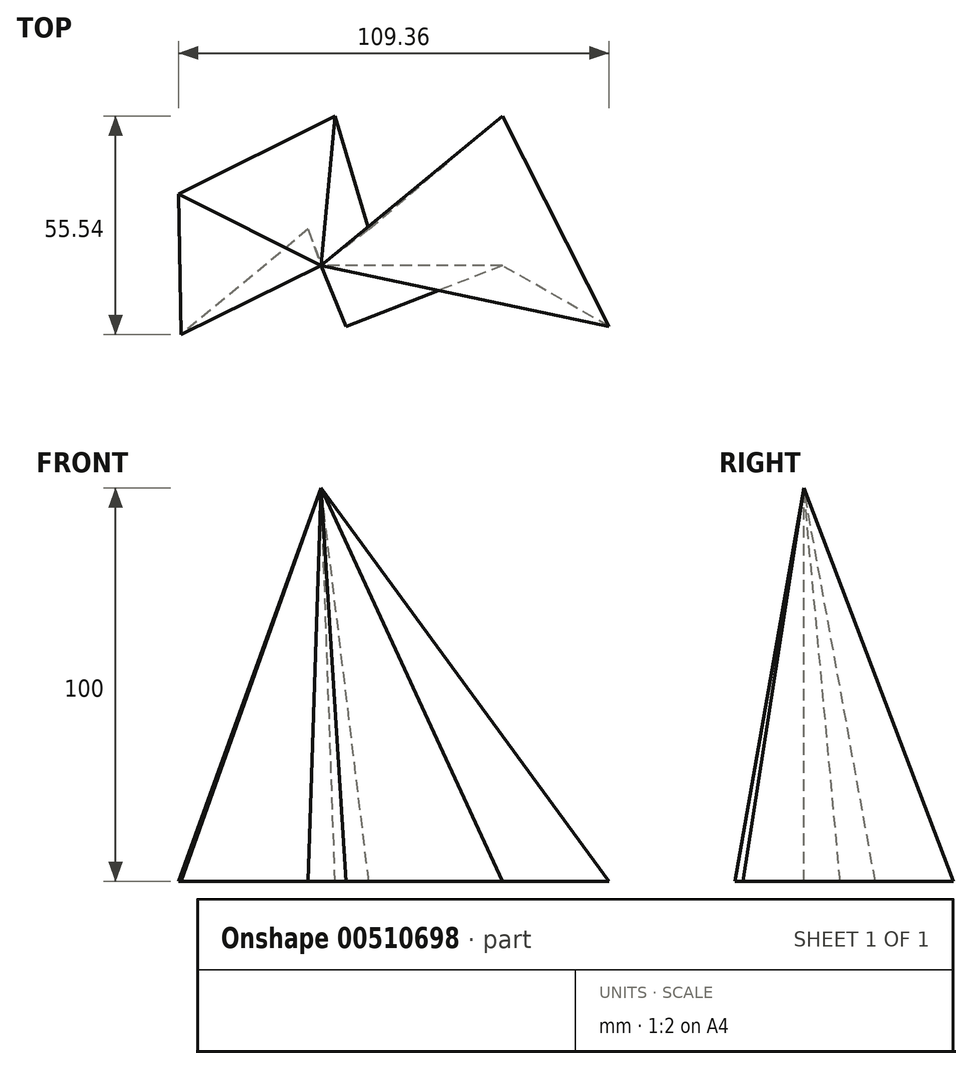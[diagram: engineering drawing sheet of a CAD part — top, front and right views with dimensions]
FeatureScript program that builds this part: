
annotation { "Feature Type Name" : "Feature", "Feature Type Description" : "" }
export const myFeature = defineFeature(function(context is Context, id is Id, definition is map)
    precondition{}
    {
        {
            var Q0;
            Q0=qCreatedBy(makeId("Top.planeOp"),FACE);
            var sketch = newSketch(context, id + "F0", { "sketchPlane" : qUnion([Q0])});
            skLineSegment(sketch, "E0", {"start": v(-57.85, -17.47) * mm, "end": v(-58.54, 18.19) * mm});
            skLineSegment(sketch, "E1", {"start": v(-58.54, 18.19) * mm, "end": v(-18.77, 38.07) * mm});
            skLineSegment(sketch, "E2", {"start": v(-18.77, 38.07) * mm, "end": v(-10.2, 9.27) * mm});
            skLineSegment(sketch, "E3", {"start": v(-10.2, 9.27) * mm, "end": v(23.73, 38.07) * mm});
            skLineSegment(sketch, "E4", {"start": v(23.73, 38.07) * mm, "end": v(50.82, -15.4) * mm});
            skLineSegment(sketch, "E5", {"start": v(50.82, -15.4) * mm, "end": v(23.73, 0) * mm});
            skLineSegment(sketch, "E6", {"start": v(23.73, 0) * mm, "end": v(-16.03, -15.4) * mm});
            skLineSegment(sketch, "E7", {"start": v(-16.03, -15.4) * mm, "end": v(-25.6, 9.27) * mm});
            skLineSegment(sketch, "E8", {"start": v(-25.6, 9.27) * mm, "end": v(-57.85, -17.47) * mm});
            skSolve(sketch);
        }
        {
            var Q0;
            Q0=qCreatedBy(makeId("Top.planeOp"),FACE);
            cPlane(context, id + "F1", {"entities" : qUnion([Q0]), "cplaneType" : CPlaneType.OFFSET, "offset" : 100 * mm, "width" : 152.4 * mm, "height" : 152.4 * mm});
        }
        {
            var Q0;
            Q0=qCreatedBy(id+"F1.planeOp",FACE);
            var sketch = newSketch(context, id + "F2", { "sketchPlane" : qUnion([Q0])});
            skPoint(sketch, "E9", {"position": v(-22.32, 0) * mm});
            skSolve(sketch);
        }
        {
            var Q0;
            Q0=makeQuery(id+"F0.imprint","IMPRINT",FACE,{"disambiguationData":[TD([[makeQuery(id+"F0.imprint","IMPRINT",EDGE,{"derivedFrom":sQuery(id+"F0.wireOp",EDGE,"E0")}),-1.0]])]});
            var Q1;
            Q1=sQuery(id+"F2.wireOp",VERTEX,"E9");
            loft(context, id + "F3", {"sheetProfilesArray" : [{ "sheetProfileEntities" : qUnion([Q0]) }, { "sheetProfileEntities" : qUnion([Q1]) }]});
        }
    });
